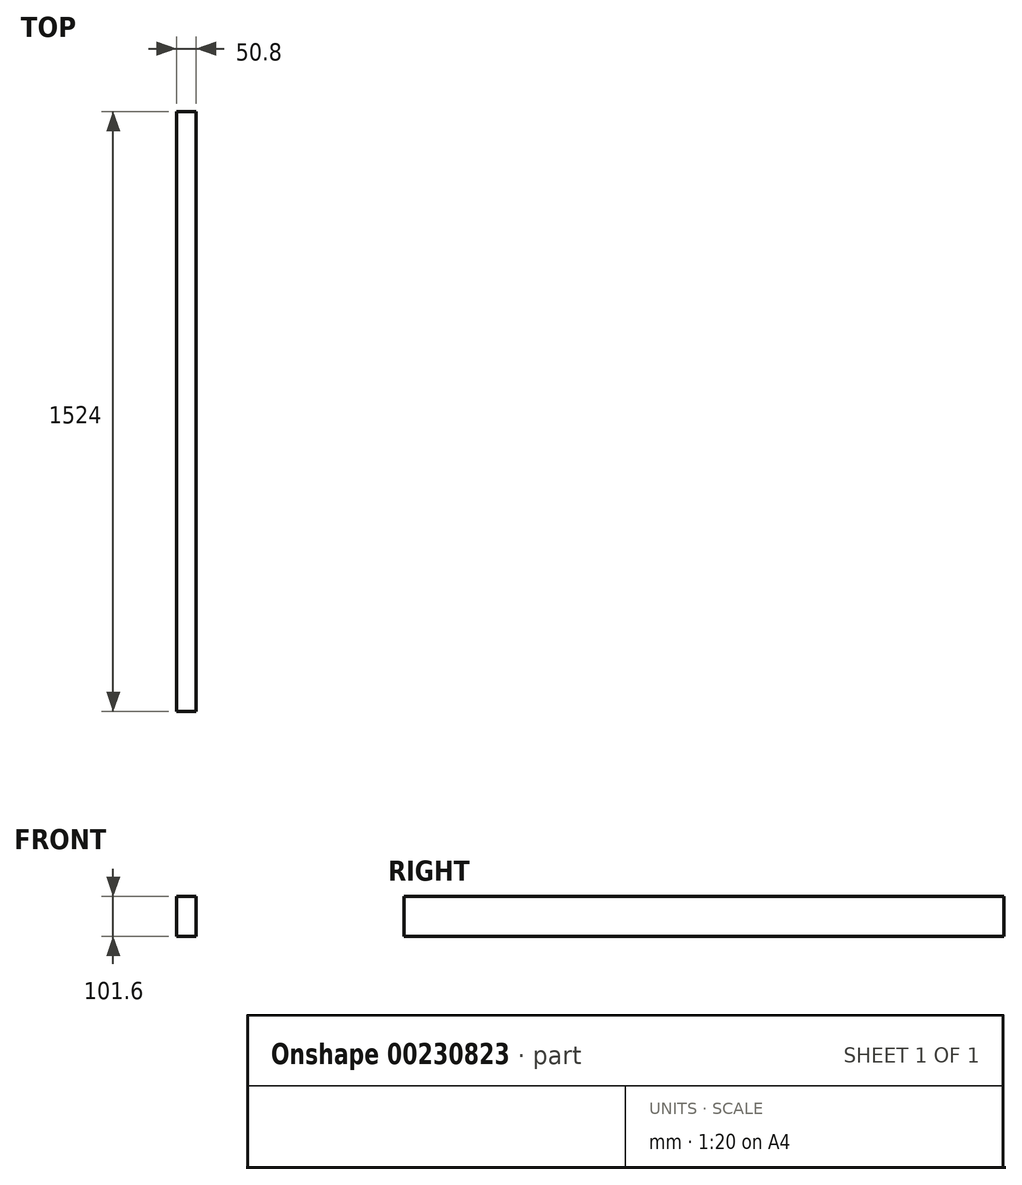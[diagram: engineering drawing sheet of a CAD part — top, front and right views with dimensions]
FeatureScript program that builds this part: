
annotation { "Feature Type Name" : "Feature", "Feature Type Description" : "" }
export const myFeature = defineFeature(function(context is Context, id is Id, definition is map)
    precondition{}
    {
        {
            var Q0;
            Q0=qCreatedBy(makeId("Right.planeOp"),FACE);
            var sketch = newSketch(context, id + "F0", { "sketchPlane" : qUnion([Q0])});
            skLineSegment(sketch, "E0.bottom", {"start": v(1437.27, 123.7) * mm, "end": v(-86.73, 123.7) * mm});
            skLineSegment(sketch, "E0.top", {"start": v(1437.27, 22.1) * mm, "end": v(-86.73, 22.1) * mm});
            skLineSegment(sketch, "E0.left", {"start": v(1437.27, 123.7) * mm, "end": v(1437.27, 22.1) * mm});
            skLineSegment(sketch, "E0.right", {"start": v(-86.73, 123.7) * mm, "end": v(-86.73, 22.1) * mm});
            skSolve(sketch);
        }
        {
            var Q0;
            Q0 = qSketchRegion(id + "F0", true);
            extrude(context, id + "F1", {"entities" : qUnion([Q0]), "depth" : 50.8 * mm});
        }
    });
